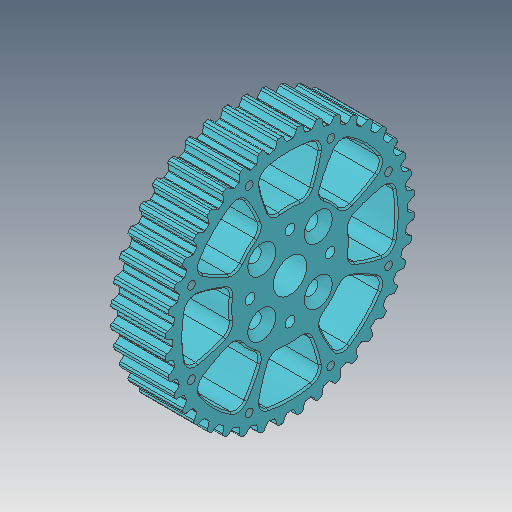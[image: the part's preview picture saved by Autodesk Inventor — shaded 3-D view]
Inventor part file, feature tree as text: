
AUTODESK INVENTOR PART (.ipt)
format: ipt  version: 2019.4 (Build 234330000, 330)  size: 681,984 bytes
history: native  units: mm
features: sketch x10, extrude x6, hole x4, fillet x2, pattern_circular x2, other x1, chamfer x1
ambient origin geometry x8: Origin, YZ Plane, XZ Plane, XY Plane, X Axis, Y Axis, Z Axis, Center Point
bodies: Body1 (feature_tree)
feature tree (26):
  other  "ソリッド1"
  extrude  "押し出し1"  Depth=1.95mm
  fillet  "フィレット1"  Radius=1.975mm
  fillet  "フィレット2"  Radius=1.11mm
  pattern_circular  "円形状パターン1"  [2 undecoded]
  extrude  "押し出し6"  Depth=37.44mm
  extrude  "押し出し2"  Depth=38.2mm
  hole  "穴1"  [1 undecoded]
  hole  "穴2"  [1 undecoded]
  hole  "穴3"  [1 undecoded]
  extrude  "押し出し3"  Depth=0.28mm
  extrude  "押し出し4"  Depth=400.0mm TaperAngle=360.0deg
  sketch  "スケッチ8"
  extrude  "押し出し5"  Depth=15.0mm
  hole  "穴4"  [1 undecoded]
  chamfer  "面取り1"  Distance=12.0mm
  pattern_circular  "円形状パターン2"  Count=4 Angle=360.0deg
  sketch  "スケッチ11"
  sketch  "スケッチ1"
  sketch  "スケッチ2"
  sketch  "スケッチ3"
  sketch  "スケッチ4"
  sketch  "スケッチ5"
  sketch  "スケッチ6"
  sketch  "スケッチ7"
  sketch  "スケッチ9"
note: 6 required parameter values undecoded (feature->parameter linkage not recoverable at this tier; creation-order binding heuristic only, values carry confidence <= 0.55)
